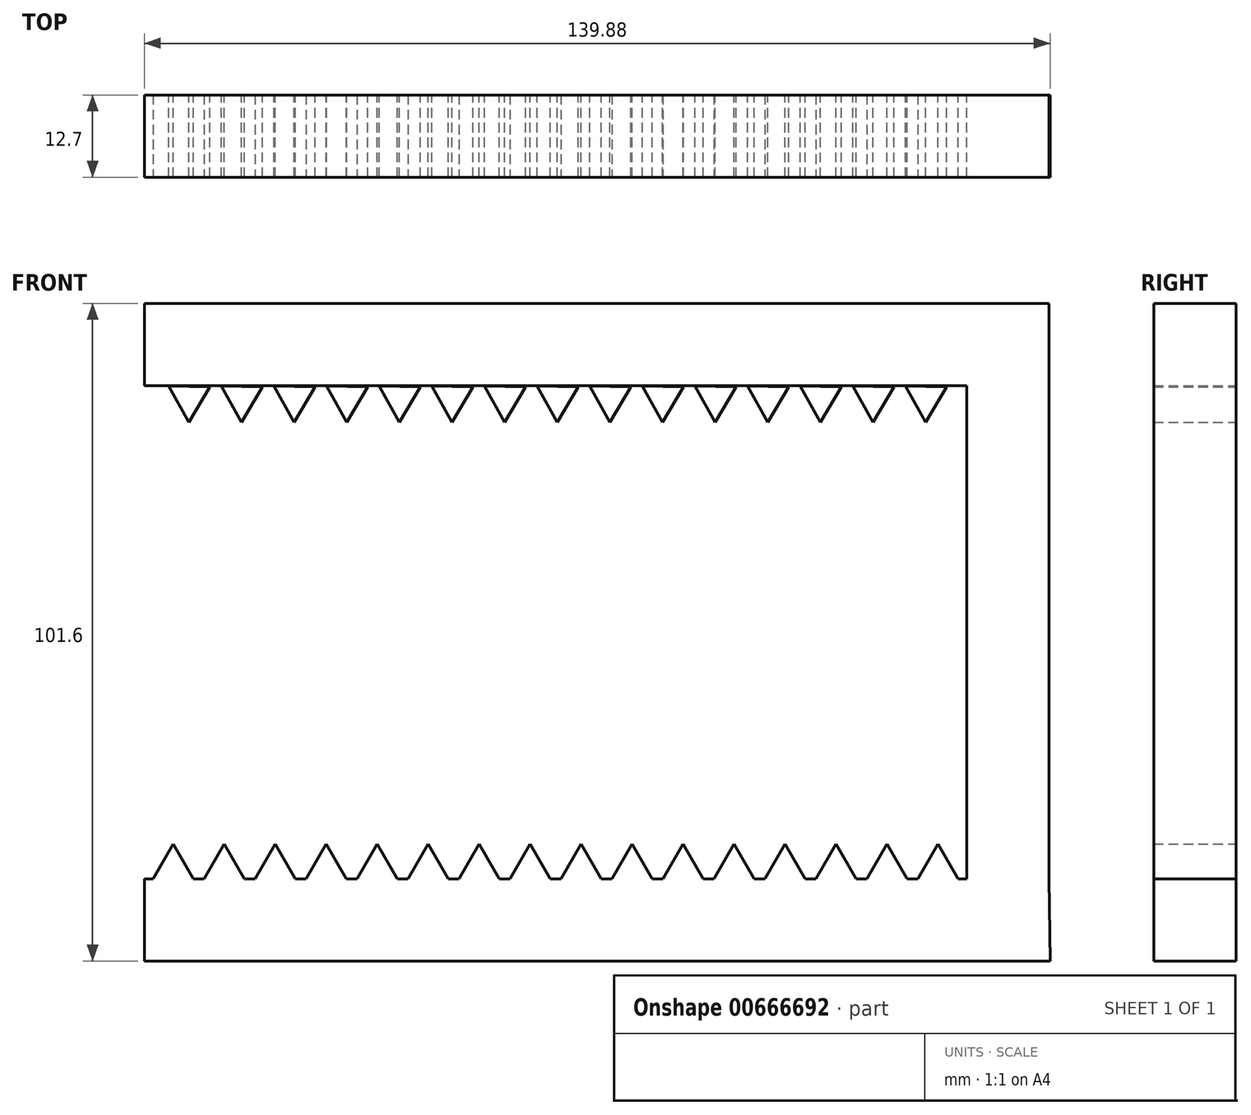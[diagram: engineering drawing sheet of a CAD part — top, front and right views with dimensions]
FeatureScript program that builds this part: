
annotation { "Feature Type Name" : "Feature", "Feature Type Description" : "" }
export const myFeature = defineFeature(function(context is Context, id is Id, definition is map)
    precondition{}
    {
        {
            var Q0;
            Q0=qCreatedBy(makeId("Front.planeOp"),FACE);
            var sketch = newSketch(context, id + "F0", { "sketchPlane" : qUnion([Q0])});
            skLineSegment(sketch, "E0", {"start": v(-61.74, 36.7) * mm, "end": v(65.26, 36.7) * mm});
            skLineSegment(sketch, "E1", {"start": v(65.26, 36.7) * mm, "end": v(65.26, -39.5) * mm});
            skLineSegment(sketch, "E2", {"start": v(65.26, -39.5) * mm, "end": v(-61.74, -39.5) * mm});
            skLineSegment(sketch, "E3", {"start": v(-61.74, 36.7) * mm, "end": v(-61.74, 49.4) * mm});
            skLineSegment(sketch, "E4", {"start": v(-61.74, 49.4) * mm, "end": v(65.26, 49.4) * mm});
            skLineSegment(sketch, "E5", {"start": v(65.26, 49.4) * mm, "end": v(65.26, 36.7) * mm});
            skLineSegment(sketch, "E6", {"start": v(65.26, 49.4) * mm, "end": v(77.96, 49.4) * mm});
            skLineSegment(sketch, "E7", {"start": v(77.96, 49.4) * mm, "end": v(77.96, -39.5) * mm});
            skLineSegment(sketch, "E8", {"start": v(77.96, -39.5) * mm, "end": v(65.26, -39.5) * mm});
            skLineSegment(sketch, "E9", {"start": v(-61.74, -39.5) * mm, "end": v(-61.74, -52.2) * mm});
            skLineSegment(sketch, "E10", {"start": v(-61.74, -52.2) * mm, "end": v(78.14, -52.2) * mm});
            skLineSegment(sketch, "E11", {"start": v(78.14, -52.2) * mm, "end": v(77.96, -39.5) * mm});
            skSolve(sketch);
        }
        {
            var Q0;
            Q0=makeQuery(id+"F0.imprint","IMPRINT",FACE,{"disambiguationData":[TD([[makeQuery(id+"F0.imprint","IMPRINT",EDGE,{"derivedFrom":sQuery(id+"F0.wireOp",EDGE,"E1")}),1.0]])]});
            var Q1;
            Q1=makeQuery(id+"F0.imprint","IMPRINT",FACE,{"disambiguationData":[TD([[makeQuery(id+"F0.imprint","IMPRINT",EDGE,{"derivedFrom":sQuery(id+"F0.wireOp",EDGE,"E0")}),1.0]])]});
            var Q2;
            Q2=makeQuery(id+"F0.imprint","IMPRINT",FACE,{"disambiguationData":[TD([[makeQuery(id+"F0.imprint","IMPRINT",EDGE,{"derivedFrom":sQuery(id+"F0.wireOp",EDGE,"E2")}),1.0]])]});
            extrude(context, id + "F1", {"entities" : qUnion([Q0, Q1, Q2]), "depth" : 12.7 * mm, "offsetDistance" : 25.4 * mm});
        }
        {
            var Q0;
            Q0=qCreatedBy(makeId("Front.planeOp"),FACE);
            var sketch = newSketch(context, id + "F2", { "sketchPlane" : qUnion([Q0])});
            skLineSegment(sketch, "E12", {"start": v(62.15, 36.51) * mm, "end": v(58.9, 31.05) * mm});
            skLineSegment(sketch, "E13", {"start": v(58.9, 31.05) * mm, "end": v(55.8, 36.58) * mm});
            skLineSegment(sketch, "E14", {"start": v(55.8, 36.58) * mm, "end": v(62.15, 36.51) * mm});
            skLineSegment(sketch, "E15.1.0.0", {"start": v(50.78, 31.05) * mm, "end": v(47.67, 36.58) * mm});
            skLineSegment(sketch, "E15.1.0.1", {"start": v(54.02, 36.51) * mm, "end": v(50.78, 31.05) * mm});
            skLineSegment(sketch, "E15.1.0.2", {"start": v(47.67, 36.58) * mm, "end": v(54.02, 36.51) * mm});
            skLineSegment(sketch, "E15.2.0.0", {"start": v(42.65, 31.05) * mm, "end": v(39.54, 36.58) * mm});
            skLineSegment(sketch, "E15.2.0.1", {"start": v(45.89, 36.51) * mm, "end": v(42.65, 31.05) * mm});
            skLineSegment(sketch, "E15.2.0.2", {"start": v(39.54, 36.58) * mm, "end": v(45.89, 36.51) * mm});
            skLineSegment(sketch, "E15.3.0.0", {"start": v(34.52, 31.05) * mm, "end": v(31.41, 36.58) * mm});
            skLineSegment(sketch, "E15.3.0.1", {"start": v(37.76, 36.51) * mm, "end": v(34.52, 31.05) * mm});
            skLineSegment(sketch, "E15.3.0.2", {"start": v(31.41, 36.58) * mm, "end": v(37.76, 36.51) * mm});
            skLineSegment(sketch, "E15.4.0.0", {"start": v(26.4, 31.05) * mm, "end": v(23.28, 36.58) * mm});
            skLineSegment(sketch, "E15.4.0.1", {"start": v(29.63, 36.51) * mm, "end": v(26.4, 31.05) * mm});
            skLineSegment(sketch, "E15.4.0.2", {"start": v(23.28, 36.58) * mm, "end": v(29.63, 36.51) * mm});
            skLineSegment(sketch, "E15.5.0.0", {"start": v(18.27, 31.05) * mm, "end": v(15.16, 36.58) * mm});
            skLineSegment(sketch, "E15.5.0.1", {"start": v(21.5, 36.51) * mm, "end": v(18.27, 31.05) * mm});
            skLineSegment(sketch, "E15.5.0.2", {"start": v(15.16, 36.58) * mm, "end": v(21.5, 36.51) * mm});
            skLineSegment(sketch, "E15.6.0.0", {"start": v(10.14, 31.05) * mm, "end": v(7.03, 36.58) * mm});
            skLineSegment(sketch, "E15.6.0.1", {"start": v(13.38, 36.51) * mm, "end": v(10.14, 31.05) * mm});
            skLineSegment(sketch, "E15.6.0.2", {"start": v(7.03, 36.58) * mm, "end": v(13.38, 36.51) * mm});
            skLineSegment(sketch, "E15.7.0.0", {"start": v(2.01, 31.05) * mm, "end": v(-1.1, 36.58) * mm});
            skLineSegment(sketch, "E15.7.0.1", {"start": v(5.25, 36.51) * mm, "end": v(2.01, 31.05) * mm});
            skLineSegment(sketch, "E15.7.0.2", {"start": v(-1.1, 36.58) * mm, "end": v(5.25, 36.51) * mm});
            skLineSegment(sketch, "E15.8.0.0", {"start": v(-6.12, 31.05) * mm, "end": v(-9.23, 36.58) * mm});
            skLineSegment(sketch, "E15.8.0.1", {"start": v(-2.88, 36.51) * mm, "end": v(-6.12, 31.05) * mm});
            skLineSegment(sketch, "E15.8.0.2", {"start": v(-9.23, 36.58) * mm, "end": v(-2.88, 36.51) * mm});
            skLineSegment(sketch, "E15.9.0.0", {"start": v(-14.24, 31.05) * mm, "end": v(-17.36, 36.58) * mm});
            skLineSegment(sketch, "E15.9.0.1", {"start": v(-11, 36.51) * mm, "end": v(-14.24, 31.05) * mm});
            skLineSegment(sketch, "E15.9.0.2", {"start": v(-17.36, 36.58) * mm, "end": v(-11, 36.51) * mm});
            skLineSegment(sketch, "E15.10.0.0", {"start": v(-22.37, 31.05) * mm, "end": v(-25.48, 36.58) * mm});
            skLineSegment(sketch, "E15.10.0.1", {"start": v(-19.13, 36.51) * mm, "end": v(-22.37, 31.05) * mm});
            skLineSegment(sketch, "E15.10.0.2", {"start": v(-25.48, 36.58) * mm, "end": v(-19.13, 36.51) * mm});
            skLineSegment(sketch, "E15.11.0.0", {"start": v(-30.5, 31.05) * mm, "end": v(-33.61, 36.58) * mm});
            skLineSegment(sketch, "E15.11.0.1", {"start": v(-27.26, 36.51) * mm, "end": v(-30.5, 31.05) * mm});
            skLineSegment(sketch, "E15.11.0.2", {"start": v(-33.61, 36.58) * mm, "end": v(-27.26, 36.51) * mm});
            skLineSegment(sketch, "E15.12.0.0", {"start": v(-38.63, 31.05) * mm, "end": v(-41.74, 36.58) * mm});
            skLineSegment(sketch, "E15.12.0.1", {"start": v(-35.4, 36.51) * mm, "end": v(-38.63, 31.05) * mm});
            skLineSegment(sketch, "E15.12.0.2", {"start": v(-41.74, 36.58) * mm, "end": v(-35.4, 36.51) * mm});
            skLineSegment(sketch, "E15.13.0.0", {"start": v(-46.76, 31.05) * mm, "end": v(-49.87, 36.58) * mm});
            skLineSegment(sketch, "E15.13.0.1", {"start": v(-43.52, 36.51) * mm, "end": v(-46.76, 31.05) * mm});
            skLineSegment(sketch, "E15.13.0.2", {"start": v(-49.87, 36.58) * mm, "end": v(-43.52, 36.51) * mm});
            skLineSegment(sketch, "E15.14.0.0", {"start": v(-54.88, 31.05) * mm, "end": v(-58, 36.58) * mm});
            skLineSegment(sketch, "E15.14.0.1", {"start": v(-51.65, 36.51) * mm, "end": v(-54.88, 31.05) * mm});
            skLineSegment(sketch, "E15.14.0.2", {"start": v(-58, 36.58) * mm, "end": v(-51.65, 36.51) * mm});
            skLineSegment(sketch, "E15.direction1", {"start": v(58.9, 31.05) * mm, "end": v(50.78, 31.05) * mm, "construction": true});
            skSolve(sketch);
        }
        {
            var Q0;
            Q0=makeQuery(id+"F2.imprint","IMPRINT",FACE,{"disambiguationData":[TD([[makeQuery(id+"F2.imprint","IMPRINT",EDGE,{"derivedFrom":sQuery(id+"F2.wireOp",EDGE,"E15.14.0.0")}),-1.0]])]});
            var Q1;
            Q1=makeQuery(id+"F2.imprint","IMPRINT",FACE,{"disambiguationData":[TD([[makeQuery(id+"F2.imprint","IMPRINT",EDGE,{"derivedFrom":sQuery(id+"F2.wireOp",EDGE,"E15.13.0.0")}),-1.0]])]});
            var Q2;
            Q2=makeQuery(id+"F2.imprint","IMPRINT",FACE,{"disambiguationData":[TD([[makeQuery(id+"F2.imprint","IMPRINT",EDGE,{"derivedFrom":sQuery(id+"F2.wireOp",EDGE,"E15.12.0.0")}),-1.0]])]});
            var Q3;
            Q3=makeQuery(id+"F2.imprint","IMPRINT",FACE,{"disambiguationData":[TD([[makeQuery(id+"F2.imprint","IMPRINT",EDGE,{"derivedFrom":sQuery(id+"F2.wireOp",EDGE,"E15.11.0.0")}),-1.0]])]});
            var Q4;
            Q4=makeQuery(id+"F2.imprint","IMPRINT",FACE,{"disambiguationData":[TD([[makeQuery(id+"F2.imprint","IMPRINT",EDGE,{"derivedFrom":sQuery(id+"F2.wireOp",EDGE,"E15.10.0.0")}),-1.0]])]});
            var Q5;
            Q5=makeQuery(id+"F2.imprint","IMPRINT",FACE,{"disambiguationData":[TD([[makeQuery(id+"F2.imprint","IMPRINT",EDGE,{"derivedFrom":sQuery(id+"F2.wireOp",EDGE,"E15.9.0.0")}),-1.0]])]});
            var Q6;
            Q6=makeQuery(id+"F2.imprint","IMPRINT",FACE,{"disambiguationData":[TD([[makeQuery(id+"F2.imprint","IMPRINT",EDGE,{"derivedFrom":sQuery(id+"F2.wireOp",EDGE,"E15.8.0.0")}),-1.0]])]});
            var Q7;
            Q7=makeQuery(id+"F2.imprint","IMPRINT",FACE,{"disambiguationData":[TD([[makeQuery(id+"F2.imprint","IMPRINT",EDGE,{"derivedFrom":sQuery(id+"F2.wireOp",EDGE,"E15.7.0.0")}),-1.0]])]});
            var Q8;
            Q8=makeQuery(id+"F2.imprint","IMPRINT",FACE,{"disambiguationData":[TD([[makeQuery(id+"F2.imprint","IMPRINT",EDGE,{"derivedFrom":sQuery(id+"F2.wireOp",EDGE,"E15.6.0.0")}),-1.0]])]});
            var Q9;
            Q9=makeQuery(id+"F2.imprint","IMPRINT",FACE,{"disambiguationData":[TD([[makeQuery(id+"F2.imprint","IMPRINT",EDGE,{"derivedFrom":sQuery(id+"F2.wireOp",EDGE,"E15.5.0.0")}),-1.0]])]});
            var Q10;
            Q10=makeQuery(id+"F2.imprint","IMPRINT",FACE,{"disambiguationData":[TD([[makeQuery(id+"F2.imprint","IMPRINT",EDGE,{"derivedFrom":sQuery(id+"F2.wireOp",EDGE,"E15.4.0.0")}),-1.0]])]});
            var Q11;
            Q11=makeQuery(id+"F2.imprint","IMPRINT",FACE,{"disambiguationData":[TD([[makeQuery(id+"F2.imprint","IMPRINT",EDGE,{"derivedFrom":sQuery(id+"F2.wireOp",EDGE,"E15.3.0.0")}),-1.0]])]});
            var Q12;
            Q12=makeQuery(id+"F2.imprint","IMPRINT",FACE,{"disambiguationData":[TD([[makeQuery(id+"F2.imprint","IMPRINT",EDGE,{"derivedFrom":sQuery(id+"F2.wireOp",EDGE,"E15.2.0.0")}),-1.0]])]});
            var Q13;
            Q13=makeQuery(id+"F2.imprint","IMPRINT",FACE,{"disambiguationData":[TD([[makeQuery(id+"F2.imprint","IMPRINT",EDGE,{"derivedFrom":sQuery(id+"F2.wireOp",EDGE,"E15.1.0.0")}),-1.0]])]});
            var Q14;
            Q14=makeQuery(id+"F2.imprint","IMPRINT",FACE,{"disambiguationData":[TD([[makeQuery(id+"F2.imprint","IMPRINT",EDGE,{"derivedFrom":sQuery(id+"F2.wireOp",EDGE,"E12")}),-1.0]])]});
            extrude(context, id + "F3", {"entities" : qUnion([Q0, Q1, Q2, Q3, Q4, Q5, Q6, Q7, Q8, Q9, Q10, Q11, Q12, Q13, Q14]), "depth" : 12.7 * mm, "offsetDistance" : 25.4 * mm});
        }
        {
            var Q0;
            Q0=qCreatedBy(makeId("Front.planeOp"),FACE);
            var sketch = newSketch(context, id + "F4", { "sketchPlane" : qUnion([Q0])});
            skLineSegment(sketch, "E16", {"start": v(64.01, -39.64) * mm, "end": v(60.84, -34.14) * mm});
            skLineSegment(sketch, "E17", {"start": v(60.84, -34.14) * mm, "end": v(57.66, -39.64) * mm});
            skLineSegment(sketch, "E18", {"start": v(57.66, -39.64) * mm, "end": v(64.01, -39.64) * mm});
            skLineSegment(sketch, "E19.1.0.0", {"start": v(52.96, -34.14) * mm, "end": v(49.79, -39.64) * mm});
            skLineSegment(sketch, "E19.1.0.1", {"start": v(56.14, -39.64) * mm, "end": v(52.96, -34.14) * mm});
            skLineSegment(sketch, "E19.1.0.2", {"start": v(49.79, -39.64) * mm, "end": v(56.14, -39.64) * mm});
            skLineSegment(sketch, "E19.2.0.0", {"start": v(45.1, -34.14) * mm, "end": v(41.92, -39.64) * mm});
            skLineSegment(sketch, "E19.2.0.1", {"start": v(48.27, -39.64) * mm, "end": v(45.1, -34.14) * mm});
            skLineSegment(sketch, "E19.2.0.2", {"start": v(41.92, -39.64) * mm, "end": v(48.27, -39.64) * mm});
            skLineSegment(sketch, "E19.3.0.0", {"start": v(37.22, -34.14) * mm, "end": v(34.04, -39.64) * mm});
            skLineSegment(sketch, "E19.3.0.1", {"start": v(40.4, -39.64) * mm, "end": v(37.22, -34.14) * mm});
            skLineSegment(sketch, "E19.3.0.2", {"start": v(34.04, -39.64) * mm, "end": v(40.4, -39.64) * mm});
            skLineSegment(sketch, "E19.4.0.0", {"start": v(29.34, -34.14) * mm, "end": v(26.17, -39.64) * mm});
            skLineSegment(sketch, "E19.4.0.1", {"start": v(32.52, -39.64) * mm, "end": v(29.34, -34.14) * mm});
            skLineSegment(sketch, "E19.4.0.2", {"start": v(26.17, -39.64) * mm, "end": v(32.52, -39.64) * mm});
            skLineSegment(sketch, "E19.5.0.0", {"start": v(21.47, -34.14) * mm, "end": v(18.3, -39.64) * mm});
            skLineSegment(sketch, "E19.5.0.1", {"start": v(24.64, -39.64) * mm, "end": v(21.47, -34.14) * mm});
            skLineSegment(sketch, "E19.5.0.2", {"start": v(18.3, -39.64) * mm, "end": v(24.64, -39.64) * mm});
            skLineSegment(sketch, "E19.6.0.0", {"start": v(13.6, -34.14) * mm, "end": v(10.42, -39.64) * mm});
            skLineSegment(sketch, "E19.6.0.1", {"start": v(16.77, -39.64) * mm, "end": v(13.6, -34.14) * mm});
            skLineSegment(sketch, "E19.6.0.2", {"start": v(10.42, -39.64) * mm, "end": v(16.77, -39.64) * mm});
            skLineSegment(sketch, "E19.7.0.0", {"start": v(5.72, -34.14) * mm, "end": v(2.55, -39.64) * mm});
            skLineSegment(sketch, "E19.7.0.1", {"start": v(8.9, -39.64) * mm, "end": v(5.72, -34.14) * mm});
            skLineSegment(sketch, "E19.7.0.2", {"start": v(2.55, -39.64) * mm, "end": v(8.9, -39.64) * mm});
            skLineSegment(sketch, "E19.8.0.0", {"start": v(-2.15, -34.14) * mm, "end": v(-5.33, -39.64) * mm});
            skLineSegment(sketch, "E19.8.0.1", {"start": v(1.02, -39.64) * mm, "end": v(-2.15, -34.14) * mm});
            skLineSegment(sketch, "E19.8.0.2", {"start": v(-5.33, -39.64) * mm, "end": v(1.02, -39.64) * mm});
            skLineSegment(sketch, "E19.9.0.0", {"start": v(-10.03, -34.14) * mm, "end": v(-13.2, -39.64) * mm});
            skLineSegment(sketch, "E19.9.0.1", {"start": v(-6.85, -39.64) * mm, "end": v(-10.03, -34.14) * mm});
            skLineSegment(sketch, "E19.9.0.2", {"start": v(-13.2, -39.64) * mm, "end": v(-6.85, -39.64) * mm});
            skLineSegment(sketch, "E19.10.0.0", {"start": v(-17.9, -34.14) * mm, "end": v(-21.08, -39.64) * mm});
            skLineSegment(sketch, "E19.10.0.1", {"start": v(-14.73, -39.64) * mm, "end": v(-17.9, -34.14) * mm});
            skLineSegment(sketch, "E19.10.0.2", {"start": v(-21.08, -39.64) * mm, "end": v(-14.73, -39.64) * mm});
            skLineSegment(sketch, "E19.11.0.0", {"start": v(-25.78, -34.14) * mm, "end": v(-28.95, -39.64) * mm});
            skLineSegment(sketch, "E19.11.0.1", {"start": v(-22.6, -39.64) * mm, "end": v(-25.78, -34.14) * mm});
            skLineSegment(sketch, "E19.11.0.2", {"start": v(-28.95, -39.64) * mm, "end": v(-22.6, -39.64) * mm});
            skLineSegment(sketch, "E19.12.0.0", {"start": v(-33.65, -34.14) * mm, "end": v(-36.82, -39.64) * mm});
            skLineSegment(sketch, "E19.12.0.1", {"start": v(-30.47, -39.64) * mm, "end": v(-33.65, -34.14) * mm});
            skLineSegment(sketch, "E19.12.0.2", {"start": v(-36.82, -39.64) * mm, "end": v(-30.47, -39.64) * mm});
            skLineSegment(sketch, "E19.13.0.0", {"start": v(-41.52, -34.14) * mm, "end": v(-44.7, -39.64) * mm});
            skLineSegment(sketch, "E19.13.0.1", {"start": v(-38.35, -39.64) * mm, "end": v(-41.52, -34.14) * mm});
            skLineSegment(sketch, "E19.13.0.2", {"start": v(-44.7, -39.64) * mm, "end": v(-38.35, -39.64) * mm});
            skLineSegment(sketch, "E19.14.0.0", {"start": v(-49.4, -34.14) * mm, "end": v(-52.57, -39.64) * mm});
            skLineSegment(sketch, "E19.14.0.1", {"start": v(-46.22, -39.64) * mm, "end": v(-49.4, -34.14) * mm});
            skLineSegment(sketch, "E19.14.0.2", {"start": v(-52.57, -39.64) * mm, "end": v(-46.22, -39.64) * mm});
            skLineSegment(sketch, "E19.15.0.0", {"start": v(-57.27, -34.14) * mm, "end": v(-60.45, -39.64) * mm});
            skLineSegment(sketch, "E19.15.0.1", {"start": v(-54.1, -39.64) * mm, "end": v(-57.27, -34.14) * mm});
            skLineSegment(sketch, "E19.15.0.2", {"start": v(-60.45, -39.64) * mm, "end": v(-54.1, -39.64) * mm});
            skLineSegment(sketch, "E19.direction1", {"start": v(57.66, -39.64) * mm, "end": v(49.79, -39.64) * mm, "construction": true});
            skSolve(sketch);
        }
        {
            var Q0;
            Q0=makeQuery(id+"F4.imprint","IMPRINT",FACE,{"disambiguationData":[TD([[makeQuery(id+"F4.imprint","IMPRINT",EDGE,{"derivedFrom":sQuery(id+"F4.wireOp",EDGE,"E19.15.0.0")}),1.0]])]});
            var Q1;
            Q1=makeQuery(id+"F4.imprint","IMPRINT",FACE,{"disambiguationData":[TD([[makeQuery(id+"F4.imprint","IMPRINT",EDGE,{"derivedFrom":sQuery(id+"F4.wireOp",EDGE,"E19.14.0.0")}),1.0]])]});
            var Q2;
            Q2=makeQuery(id+"F4.imprint","IMPRINT",FACE,{"disambiguationData":[TD([[makeQuery(id+"F4.imprint","IMPRINT",EDGE,{"derivedFrom":sQuery(id+"F4.wireOp",EDGE,"E19.13.0.0")}),1.0]])]});
            var Q3;
            Q3=makeQuery(id+"F4.imprint","IMPRINT",FACE,{"disambiguationData":[TD([[makeQuery(id+"F4.imprint","IMPRINT",EDGE,{"derivedFrom":sQuery(id+"F4.wireOp",EDGE,"E19.12.0.0")}),1.0]])]});
            var Q4;
            Q4=makeQuery(id+"F4.imprint","IMPRINT",FACE,{"disambiguationData":[TD([[makeQuery(id+"F4.imprint","IMPRINT",EDGE,{"derivedFrom":sQuery(id+"F4.wireOp",EDGE,"E19.11.0.0")}),1.0]])]});
            var Q5;
            Q5=makeQuery(id+"F4.imprint","IMPRINT",FACE,{"disambiguationData":[TD([[makeQuery(id+"F4.imprint","IMPRINT",EDGE,{"derivedFrom":sQuery(id+"F4.wireOp",EDGE,"E19.10.0.0")}),1.0]])]});
            var Q6;
            Q6=makeQuery(id+"F4.imprint","IMPRINT",FACE,{"disambiguationData":[TD([[makeQuery(id+"F4.imprint","IMPRINT",EDGE,{"derivedFrom":sQuery(id+"F4.wireOp",EDGE,"E19.9.0.0")}),1.0]])]});
            var Q7;
            Q7=makeQuery(id+"F4.imprint","IMPRINT",FACE,{"disambiguationData":[TD([[makeQuery(id+"F4.imprint","IMPRINT",EDGE,{"derivedFrom":sQuery(id+"F4.wireOp",EDGE,"E19.8.0.0")}),1.0]])]});
            var Q8;
            Q8=makeQuery(id+"F4.imprint","IMPRINT",FACE,{"disambiguationData":[TD([[makeQuery(id+"F4.imprint","IMPRINT",EDGE,{"derivedFrom":sQuery(id+"F4.wireOp",EDGE,"E19.7.0.0")}),1.0]])]});
            var Q9;
            Q9=makeQuery(id+"F4.imprint","IMPRINT",FACE,{"disambiguationData":[TD([[makeQuery(id+"F4.imprint","IMPRINT",EDGE,{"derivedFrom":sQuery(id+"F4.wireOp",EDGE,"E19.6.0.0")}),1.0]])]});
            var Q10;
            Q10=makeQuery(id+"F4.imprint","IMPRINT",FACE,{"disambiguationData":[TD([[makeQuery(id+"F4.imprint","IMPRINT",EDGE,{"derivedFrom":sQuery(id+"F4.wireOp",EDGE,"E19.5.0.0")}),1.0]])]});
            var Q11;
            Q11=makeQuery(id+"F4.imprint","IMPRINT",FACE,{"disambiguationData":[TD([[makeQuery(id+"F4.imprint","IMPRINT",EDGE,{"derivedFrom":sQuery(id+"F4.wireOp",EDGE,"E19.3.0.0")}),1.0]])]});
            var Q12;
            Q12=makeQuery(id+"F4.imprint","IMPRINT",FACE,{"disambiguationData":[TD([[makeQuery(id+"F4.imprint","IMPRINT",EDGE,{"derivedFrom":sQuery(id+"F4.wireOp",EDGE,"E19.2.0.0")}),1.0]])]});
            var Q13;
            Q13=makeQuery(id+"F4.imprint","IMPRINT",FACE,{"disambiguationData":[TD([[makeQuery(id+"F4.imprint","IMPRINT",EDGE,{"derivedFrom":sQuery(id+"F4.wireOp",EDGE,"E19.1.0.0")}),1.0]])]});
            var Q14;
            Q14=makeQuery(id+"F4.imprint","IMPRINT",FACE,{"disambiguationData":[TD([[makeQuery(id+"F4.imprint","IMPRINT",EDGE,{"derivedFrom":sQuery(id+"F4.wireOp",EDGE,"E16")}),1.0]])]});
            var Q15;
            Q15=makeQuery(id+"F4.imprint","IMPRINT",FACE,{"disambiguationData":[TD([[makeQuery(id+"F4.imprint","IMPRINT",EDGE,{"derivedFrom":sQuery(id+"F4.wireOp",EDGE,"E19.4.0.0")}),1.0]])]});
            extrude(context, id + "F5", {"entities" : qUnion([Q0, Q1, Q2, Q3, Q4, Q5, Q6, Q7, Q8, Q9, Q10, Q11, Q12, Q13, Q14, Q15]), "operationType" : NewBodyOperationType.ADD, "depth" : 12.7 * mm, "offsetDistance" : 25.4 * mm});
        }
    });
